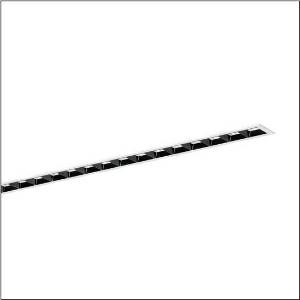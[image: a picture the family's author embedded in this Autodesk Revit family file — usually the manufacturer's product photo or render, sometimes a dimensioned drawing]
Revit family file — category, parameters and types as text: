
# Revit family: silica_r__21_51mx14tctaw_e0ea
name_source: partatom
category: Lighting Fixtures
units: mm (PartAtom-declared; Revit-internal decimal feet)

## family parameters
Cut with Voids When Loaded = No
Host = Face
Light Source = No
Part Type = Normal
Room Calculation Point = No
Round Connector Dimension = Use Diameter
Shared = No

## types (1)
- --- (1 x LED, 8200 lm, 81.1 W, 6500K)
    Apparent Load = 81 VA
    CIE Flux Codes = 74 94 99 100 100
    Color Rendering = 80
    Color Temperature = 6500K
    Default Elevation = 1800 mm
    Description = Silica® 21, office luminaire, primary light control with darklight reflector, of PMMA, black, light emission: direct distribution, primary light characteristic: asymmetric, installation type: recessed, LED, rated luminous flux: 8.200lm, luminous efficacy: 96lm/W, light colour: 8tw, colour temperature: 2700..6500K, control gear: DALI DT8, with terminal, 3+2-pole, max. 2.5mm², mains connection: 220..240V, AC, 50/60Hz, rated input power: 85.2W, luminaire housing, of aluminium, traffic white (RAL 9016), length: 3.028mm, width: 79mm, height: 53mm, protection rating (complete): IP20, insulation class (complete): insulation class I (protective earthing), certification: CE, ENEC, VDE, permissible operating ambient temperature: 0..+35°C, standard: EN 50419, packaging unit: 1 piece
    Height = 0 mm  [stored 0 ft]
    Lamp = 1 x LED
    Lamp Light Flux = 8200 lm
    Lamp Power = 81.1 W
    Lamp count = 1
    Length = 3027 mm
    Luminous efficacy = 101 lm/W
    Manufacturer = Siteco
    ModVariant = No
    Model = 51MX14TCTAW
    Mounting Place = Ceiling
    Mounting Type = Recessed
    Number of Poles = 1
    OnlyDefault = Yes
    Power Factor = 1
    Product Name = Silica® 21
    Product group = office luminaire | ceiling recessed
    ProductGroupID = 401
    Protection Class = Protection class I
    Protection Degree = IP 20
    RLX_Detail_Level = 1
    RLX_Emergency_Light_Flux = 0 lm
    RLX_Emergency_Type = 0
    RLX_Emergency_Type_DB = No
    RlxData = <blob elided: 59481 chars, md5=f95b2630>
    Socket = socket
    Standby Power = 0 W
    System Light Flux = 8200 lm
    System Power = 81 W
    Type Comments = individual setting
    Type Image = l_1335880.jpg
    URL = http://relux.com
    VarID = @adj_140022
    Voltage = 0 V
    Weight = 0.00 kg
    Width = 79 mm

note: [stored X ft] marks values corroborated as IEEE doubles in the binary element streams (Revit-internal decimal feet)

## geometry (parser evidence)
native form markers: Blend x4, Sweep x10
no freeform markers — native parametric forms only
